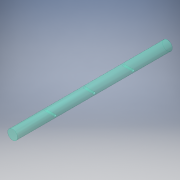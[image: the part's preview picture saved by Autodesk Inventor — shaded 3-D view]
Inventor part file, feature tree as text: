
AUTODESK INVENTOR PART (.ipt)
format: ipt  version: 2016 (Build 200138000, 138)  size: 123,392 bytes
history: native  units: in
note: dims shown in document units (in); Inventor stores cm internally (conversion verified against a paired STEP export)
features: extrude x3, sketch x2
ambient origin geometry x8: Origin, YZ Plane, XZ Plane, XY Plane, X Axis, Y Axis, Z Axis, Center Point
bodies: Solid1 (feature_tree)
feature tree (5):
  extrude  "Extrusion1"  Depth=8.0in TaperAngle=0.0deg
  extrude  "Extrusion8"  Depth=0.05in
  extrude  "Extrusion9"  Depth=2.0in
  sketch  "Sketch1"  dims[d0=0.5in d1=8.0in d2=0.0in]
  sketch  "Sketch7"  dims[d20=0.06in d21=0.05in d26=0.5in d27=0.06in d42=2.0in d43=0.1in d44=2.0in d45=0.1in d46=2.0in d47=0.1in d48=1.0in d49=0.0in d50=1.0in d51=0.0in]
